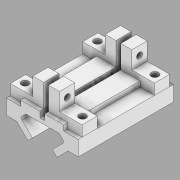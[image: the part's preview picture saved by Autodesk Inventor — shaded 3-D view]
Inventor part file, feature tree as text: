
AUTODESK INVENTOR PART (.ipt)
format: ipt  version: 2020 (Build 240168000, 168)  size: 392,704 bytes
history: native  units: in
note: dims shown in document units (in); Inventor stores cm internally (conversion verified against a paired STEP export)
features: extrude x8, projected_geometry x8, sketch x7, plane x4, mirror x3, other x2, fillet x1
ambient origin geometry x8: Origin, YZ Plane, XZ Plane, XY Plane, X Axis, Y Axis, Z Axis, Center Point
bodies: Solid3 (feature_tree)
feature tree (33):
  extrude  "Carriage Frame"  Depth=1.0in
  fillet  "Fillet1"  Radius=0.2756in
  sketch  "Sketch7"  dims[d16=5.0in d17=0.0in]
  extrude  "Carriage Screw"  TaperAngle=0.0deg  [1 undecoded]
  extrude  "Carriage Screw Insert"  Depth=0.125in
  other  "Ball Bearings"
  other  "Carriage Mid Plane"
  extrude  "Ball Bearing Hole"  Depth=0.5725in
  mirror  "Mirror4"
  extrude  "Extrusion11"  Depth=0.25in TaperAngle=0.0deg
  plane  "Work Plane3"
  extrude  "Extrusion12"  Depth=0.315in
  extrude  "Extrusion13"  Depth=0.25in
  extrude  "Extrusion14"  Depth=0.25in TaperAngle=0.0deg
  plane  "Work Plane4"
  plane  "Work Plane5"
  mirror  "Mirror5"
  mirror  "Mirror6"
  plane  "Work Plane2"
  sketch  "Sketch12"  dims[d60=0.125in d61=0.6in]
  sketch  "Sketch1"  dims[d2=1.0in d3=1.0in d6=0.8661in d14=0.2756in]
  projected_geometry  "Projected Loop13"
  projected_geometry  "Projected Loop14"
  projected_geometry  "Projected Loop15"
  projected_geometry  "Projected Loop17"
  projected_geometry  "Projected Loop19"
  sketch  "Sketch13"  dims[d78=0.5725in d79=0.378in]
  projected_geometry  "Projected Loop20"
  sketch  "Sketch15"  dims[d80=0.0in d81=0.0in d82=0.25in d83=0.0in]
  projected_geometry  "Projected Loop22"
  sketch  "Sketch16"  dims[d92=0.315in d94=0.315in]
  sketch  "Sketch17"  dims[d106=1.3in d107=0.3in d110=0.06in d111=0.0in d112=0.25in d113=1.6in d114=0.0in d115=-0.6in d116=0.8in d117=0.0in d118=0.0in d119=0.0in d120=1.0in d121=0.0in d122=0.315in d123=0.0in d124=0.0in d26=0.5in d27=0.0344in d28=0.5in d29=0.0344in d30=0.25in d31=0.375in d32=0.5635in d33=0.75in d34=0.8108in d35=0.0625in d36=0.75in d37=0.375in]
  projected_geometry  "Projected Loop23"
note: 1 required parameter value undecoded (feature->parameter linkage not recoverable at this tier; creation-order binding heuristic only, values carry confidence <= 0.55)
